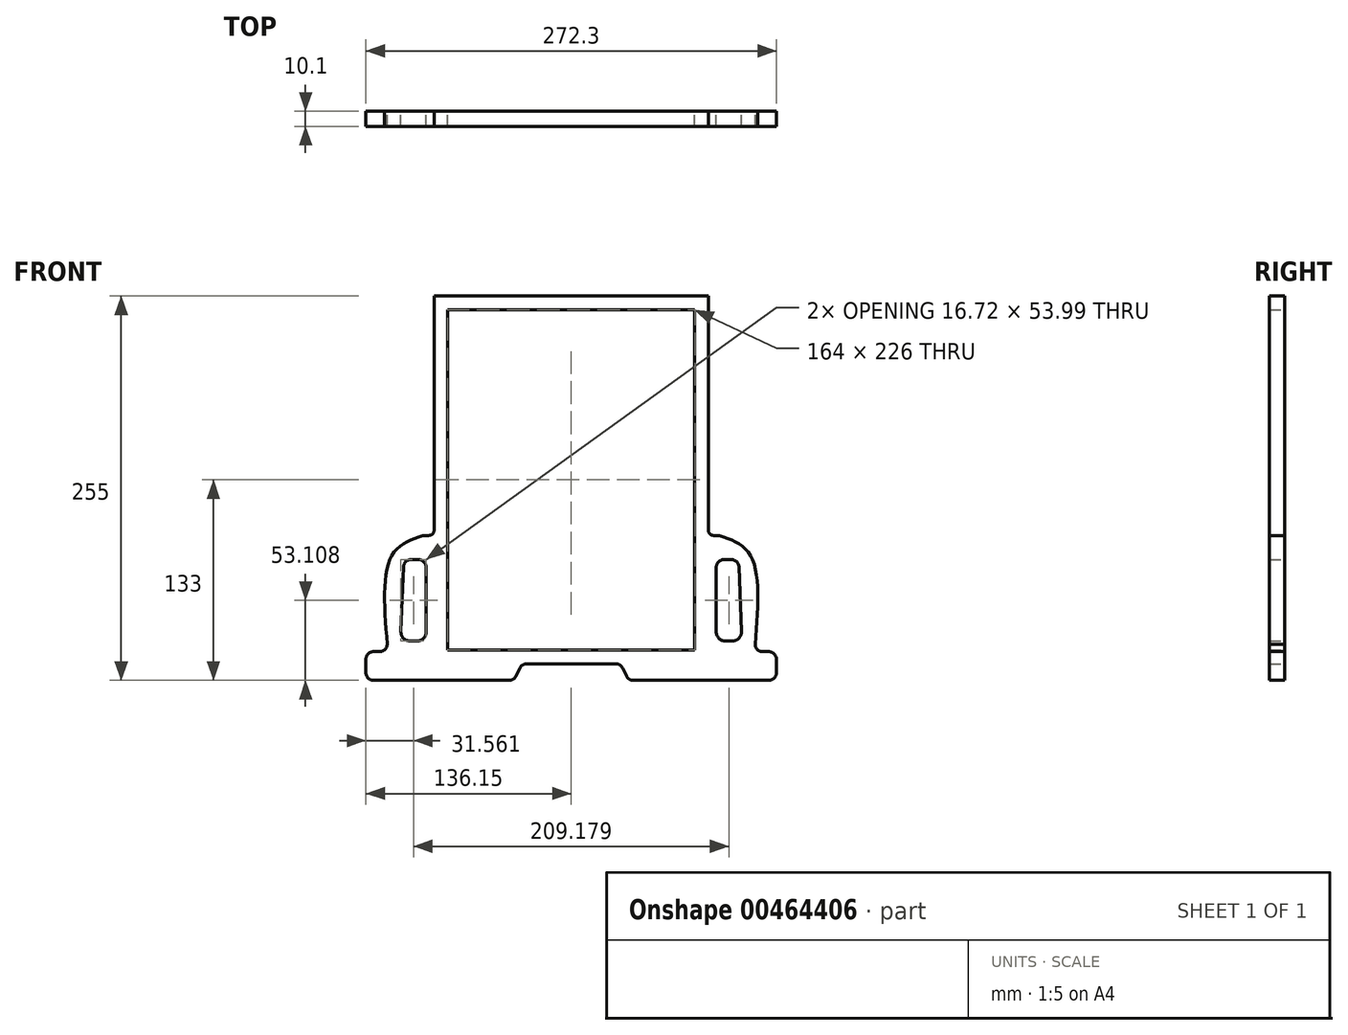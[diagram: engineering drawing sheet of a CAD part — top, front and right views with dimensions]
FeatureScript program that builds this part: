
annotation { "Feature Type Name" : "Feature", "Feature Type Description" : "" }
export const myFeature = defineFeature(function(context is Context, id is Id, definition is map)
    precondition{}
    {
        {
            var Q0;
            Q0=qCreatedBy(makeId("Front.planeOp"),FACE);
            var sketch = newSketch(context, id + "F0", { "sketchPlane" : qUnion([Q0])});
            skLineSegment(sketch, "E0.bottom", {"start": v(-82, -113) * mm, "end": v(82, -113) * mm});
            skLineSegment(sketch, "E0.top", {"start": v(-82, 113) * mm, "end": v(82, 113) * mm});
            skLineSegment(sketch, "E0.left", {"start": v(-82, -113) * mm, "end": v(-82, 113) * mm});
            skLineSegment(sketch, "E0.right", {"start": v(82, -113) * mm, "end": v(82, 113) * mm});
            skPoint(sketch, "E0.middle", {"position": v(0, 0) * mm});
            skLineSegment(sketch, "E1", {"start": v(-131.15, -133) * mm, "end": v(-41.15, -133) * mm});
            skLineSegment(sketch, "E2.0", {"start": v(-91, 122) * mm, "end": v(91, 122) * mm});
            skLineSegment(sketch, "E2.1", {"start": v(-91, -33.6) * mm, "end": v(-91, 122) * mm});
            skLineSegment(sketch, "E2.2", {"start": v(-29.57, -122) * mm, "end": v(29.57, -122) * mm});
            skLineSegment(sketch, "E2.3", {"start": v(91, -33.6) * mm, "end": v(91, 122) * mm});
            skLineSegment(sketch, "E3", {"start": v(-36.65, -130.17) * mm, "end": v(-34.07, -124.83) * mm});
            skLineSegment(sketch, "E4.trimOffspring", {"start": v(41.15, -133) * mm, "end": v(131.15, -133) * mm});
            skLineSegment(sketch, "E5.MirrorCS", {"start": v(36.65, -130.17) * mm, "end": v(34.07, -124.83) * mm});
            skPoint(sketch, "E6.newPointA", {"position": v(-32.7, -122) * mm});
            skArc(sketch, "E6.filletArc", {"start": v(-29.57, -122) * mm, "mid": v(-32.22, -122.77) * mm, "end": v(-34.07, -124.83) * mm});
            skPoint(sketch, "E7.newPointA", {"position": v(32.7, -122) * mm});
            skArc(sketch, "E7.filletArc", {"start": v(34.07, -124.83) * mm, "mid": v(32.22, -122.77) * mm, "end": v(29.57, -122) * mm});
            skPoint(sketch, "E8.visualSharp", {"position": v(38.01, -133) * mm});
            skArc(sketch, "E8.filletArc", {"start": v(36.65, -130.17) * mm, "mid": v(38.5, -132.23) * mm, "end": v(41.15, -133) * mm});
            skPoint(sketch, "E9.visualSharp", {"position": v(-38.01, -133) * mm});
            skArc(sketch, "E9.filletArc", {"start": v(-41.15, -133) * mm, "mid": v(-38.5, -132.23) * mm, "end": v(-36.65, -130.17) * mm});
            skLineSegment(sketch, "E10", {"start": v(97.75, -36.87) * mm, "end": v(94.27, -36.87) * mm});
            skLineSegment(sketch, "E11", {"start": v(136.15, -128) * mm, "end": v(136.15, -118.94) * mm});
            skLineSegment(sketch, "E12", {"start": v(131.15, -113.94) * mm, "end": v(127.06, -113.94) * mm});
            skPoint(sketch, "E13.visualSharp", {"position": v(136.15, -133) * mm});
            skArc(sketch, "E13.filletArc", {"start": v(131.15, -133) * mm, "mid": v(134.69, -131.54) * mm, "end": v(136.15, -128) * mm});
            skPoint(sketch, "E14.visualSharp", {"position": v(136.15, -113.94) * mm});
            skArc(sketch, "E14.filletArc", {"start": v(136.15, -118.94) * mm, "mid": v(134.69, -115.4) * mm, "end": v(131.15, -113.94) * mm});
            skArc(sketch, "E15.filletArc", {"start": v(122.06, -108.94) * mm, "mid": v(123.52, -112.48) * mm, "end": v(127.06, -113.94) * mm});
            skFitSpline(sketch, "E16", {"points": [v(122.06, -108.94) * mm, v(118.8, -49.94) * mm, v(97.75, -36.87) * mm], "startDerivative": vector(9.26, 116.63) * mm, "endDerivative": vector(-63.04, 20.7) * mm});
            skArc(sketch, "E17.filletArc", {"start": v(91, -33.6) * mm, "mid": v(91.96, -35.9) * mm, "end": v(94.27, -36.87) * mm});
            skArc(sketch, "E18.MirrorCS", {"start": v(-91, -33.6) * mm, "mid": v(-91.96, -35.9) * mm, "end": v(-94.27, -36.87) * mm});
            skLineSegment(sketch, "E19.MirrorCS", {"start": v(-97.75, -36.87) * mm, "end": v(-94.27, -36.87) * mm});
            skFitSpline(sketch, "E20.MirrorCS", {"points": [v(-122.06, -108.94) * mm, v(-118.8, -49.94) * mm, v(-97.75, -36.87) * mm], "startDerivative": vector(-9.26, 116.63) * mm, "endDerivative": vector(63.04, 20.7) * mm});
            skLineSegment(sketch, "E21.MirrorCS", {"start": v(-136.15, -128) * mm, "end": v(-136.15, -118.94) * mm});
            skLineSegment(sketch, "E22.MirrorCS", {"start": v(-131.15, -113.94) * mm, "end": v(-127.06, -113.94) * mm});
            skArc(sketch, "E23.MirrorCS", {"start": v(-122.06, -108.94) * mm, "mid": v(-123.52, -112.48) * mm, "end": v(-127.06, -113.94) * mm});
            skArc(sketch, "E24.MirrorCS", {"start": v(-131.15, -133) * mm, "mid": v(-134.69, -131.54) * mm, "end": v(-136.15, -128) * mm});
            skArc(sketch, "E25.MirrorCS", {"start": v(-136.15, -118.94) * mm, "mid": v(-134.69, -115.4) * mm, "end": v(-131.15, -113.94) * mm});
            skPoint(sketch, "E26.orphan", {"position": v(-107.06, -36.87) * mm});
            skPoint(sketch, "E27.orphan", {"position": v(111.1, -36.87) * mm});
            skLineSegment(sketch, "E28", {"start": v(96.23, -57.9) * mm, "end": v(96.23, -100.89) * mm});
            skLineSegment(sketch, "E29", {"start": v(101.23, -52.9) * mm, "end": v(106.29, -52.9) * mm});
            skLineSegment(sketch, "E30", {"start": v(111.29, -57.7) * mm, "end": v(112.95, -100.66) * mm});
            skPoint(sketch, "E31.visualSharp", {"position": v(96.23, -52.9) * mm});
            skArc(sketch, "E31.filletArc", {"start": v(101.23, -52.9) * mm, "mid": v(97.7, -54.36) * mm, "end": v(96.23, -57.9) * mm});
            skPoint(sketch, "E32.visualSharp", {"position": v(111.1, -52.9) * mm});
            skArc(sketch, "E32.filletArc", {"start": v(111.29, -57.7) * mm, "mid": v(109.76, -54.3) * mm, "end": v(106.29, -52.9) * mm});
            skLineSegment(sketch, "E33", {"start": v(102.23, -106.89) * mm, "end": v(106.95, -106.89) * mm});
            skPoint(sketch, "E34.visualSharp", {"position": v(96.23, -106.89) * mm});
            skArc(sketch, "E34.filletArc", {"start": v(96.23, -100.89) * mm, "mid": v(97.99, -105.13) * mm, "end": v(102.23, -106.89) * mm});
            skArc(sketch, "E35.filletArc", {"start": v(106.95, -106.89) * mm, "mid": v(111.28, -105.05) * mm, "end": v(112.95, -100.66) * mm});
            skLineSegment(sketch, "E36.MirrorCS", {"start": v(-111.29, -57.7) * mm, "end": v(-112.95, -100.66) * mm});
            skArc(sketch, "E37.MirrorCS", {"start": v(-111.29, -57.7) * mm, "mid": v(-109.76, -54.3) * mm, "end": v(-106.29, -52.9) * mm});
            skLineSegment(sketch, "E38.MirrorCS", {"start": v(-101.23, -52.9) * mm, "end": v(-106.29, -52.9) * mm});
            skLineSegment(sketch, "E39.MirrorCS", {"start": v(-96.23, -57.9) * mm, "end": v(-96.23, -100.89) * mm});
            skArc(sketch, "E40.MirrorCS", {"start": v(-101.23, -52.9) * mm, "mid": v(-97.7, -54.36) * mm, "end": v(-96.23, -57.9) * mm});
            skArc(sketch, "E41.MirrorCS", {"start": v(-96.23, -100.89) * mm, "mid": v(-97.99, -105.13) * mm, "end": v(-102.23, -106.89) * mm});
            skLineSegment(sketch, "E42.MirrorCS", {"start": v(-102.23, -106.89) * mm, "end": v(-106.95, -106.89) * mm});
            skArc(sketch, "E43.MirrorCS", {"start": v(-106.95, -106.89) * mm, "mid": v(-111.28, -105.05) * mm, "end": v(-112.95, -100.66) * mm});
            skSolve(sketch);
        }
        {
            var Q0;
            Q0=makeQuery(id+"F0.imprint","IMPRINT",FACE,{"disambiguationData":[TD([[makeQuery(id+"F0.imprint","IMPRINT",EDGE,{"derivedFrom":sQuery(id+"F0.wireOp",EDGE,"E0.bottom")}),-1.0]])]});
            extrude(context, id + "F1", {"entities" : qUnion([Q0]), "endBound" : BoundingType.SYMMETRIC, "depth" : 10.1 * mm});
        }
        {
            var Q0;
            Q0=makeQuery(id+"F1.opExtrude","SWEPT_EDGE",EDGE,{"disambiguationData":[OSD([sQuery(id+"F0.wireOp",EDGE,"E10"),sQuery(id+"F0.wireOp",EDGE,"E16")])]});
            fillet(context, id + "F2", {"entities" : qUnion([Q0]), "radius" : 5 * mm, "tangentPropagation" : true, "allowEdgeOverflow" : false});
        }
        {
            var Q0;
            Q0=makeQuery(id+"F1.opExtrude","SWEPT_EDGE",EDGE,{"disambiguationData":[OSD([sQuery(id+"F0.wireOp",EDGE,"E19.MirrorCS"),sQuery(id+"F0.wireOp",EDGE,"E20.MirrorCS")])]});
            fillet(context, id + "F3", {"entities" : qUnion([Q0]), "radius" : 5 * mm, "tangentPropagation" : true, "allowEdgeOverflow" : false});
        }
    });
